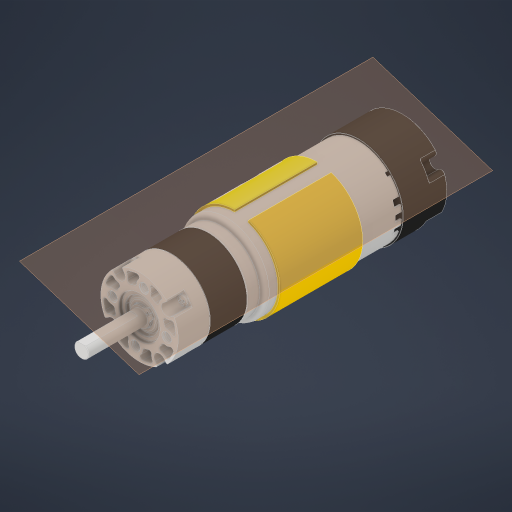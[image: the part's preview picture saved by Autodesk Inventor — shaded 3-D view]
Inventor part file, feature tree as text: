
AUTODESK INVENTOR PART (.ipt)
format: ipt  version: 2023 (Build 270158000, 158)  size: 4,847,104 bytes
history: imported  units: in
note: dims shown in document units (in); Inventor stores cm internally (conversion verified against a paired STEP export)
features: other x2, plane x1, sketch x1, imported_body x1
ambient origin geometry x8: Origin, YZ Plane, XZ Plane, XY Plane, X Axis, Y Axis, Z Axis, Center Point
bodies: Solid1 (imported_parasolid), Solid2 (imported_parasolid), Solid3 (imported_parasolid), Solid4 (imported_parasolid), Solid5 (imported_parasolid), Solid6 (imported_parasolid), Solid7 (imported_parasolid), Solid8 (imported_parasolid), Solid9 (imported_parasolid), Solid10 (imported_parasolid), Solid11 (imported_parasolid), Solid12 (imported_parasolid), Solid13 (imported_parasolid), Solid14 (imported_parasolid), Solid15 (imported_parasolid), Solid16 (imported_parasolid), Solid17 (imported_parasolid), Solid18 (imported_parasolid), Solid19 (imported_parasolid), Solid20 (imported_parasolid), Solid21 (imported_parasolid), Solid22 (imported_parasolid), Solid23 (imported_parasolid), Solid24 (imported_parasolid), Solid25 (imported_parasolid), Solid26 (imported_parasolid), Solid27 (imported_parasolid), Solid28 (imported_parasolid), Solid29 (imported_parasolid), Solid30 (imported_parasolid), Solid31 (imported_parasolid), Solid32 (imported_parasolid), Solid33 (imported_parasolid), Solid34 (imported_parasolid), Solid35 (imported_parasolid), Solid36 (imported_parasolid), Solid37 (imported_parasolid), Solid38 (imported_parasolid), Body1 (imported_parasolid), Body2 (imported_parasolid), Body3 (imported_parasolid), Body4 (imported_parasolid), Body5 (imported_parasolid), Body6 (imported_parasolid), Body7 (imported_parasolid), Body8 (imported_parasolid), Body9 (imported_parasolid), Body10 (imported_parasolid), Body11 (imported_parasolid), Body12 (imported_parasolid), Body13 (imported_parasolid), Body14 (imported_parasolid), Body15 (imported_parasolid), Body16 (imported_parasolid), Body17 (imported_parasolid), Body18 (imported_parasolid), Body19 (imported_parasolid), Body20 (imported_parasolid), Body21 (imported_parasolid), Body22 (imported_parasolid), Body23 (imported_parasolid), Body24 (imported_parasolid), Body25 (imported_parasolid), Body26 (imported_parasolid), Body27 (imported_parasolid), Body28 (imported_parasolid), Body29 (imported_parasolid), Body30 (imported_parasolid), Body31 (imported_parasolid), Body32 (imported_parasolid), Body33 (imported_parasolid), Body34 (imported_parasolid), Body35 (imported_parasolid), Body36 (imported_parasolid), Body37 (imported_parasolid), Body38 (imported_parasolid)
feature tree (5):
  plane  "Work Plane1"
  other  "Decal1"
  sketch  "Sketch1"
  other  "Image1"
  imported_body  NMx_Import_Brep_tag  [imported B-rep: ~144 faces, bbox_mm=None]
